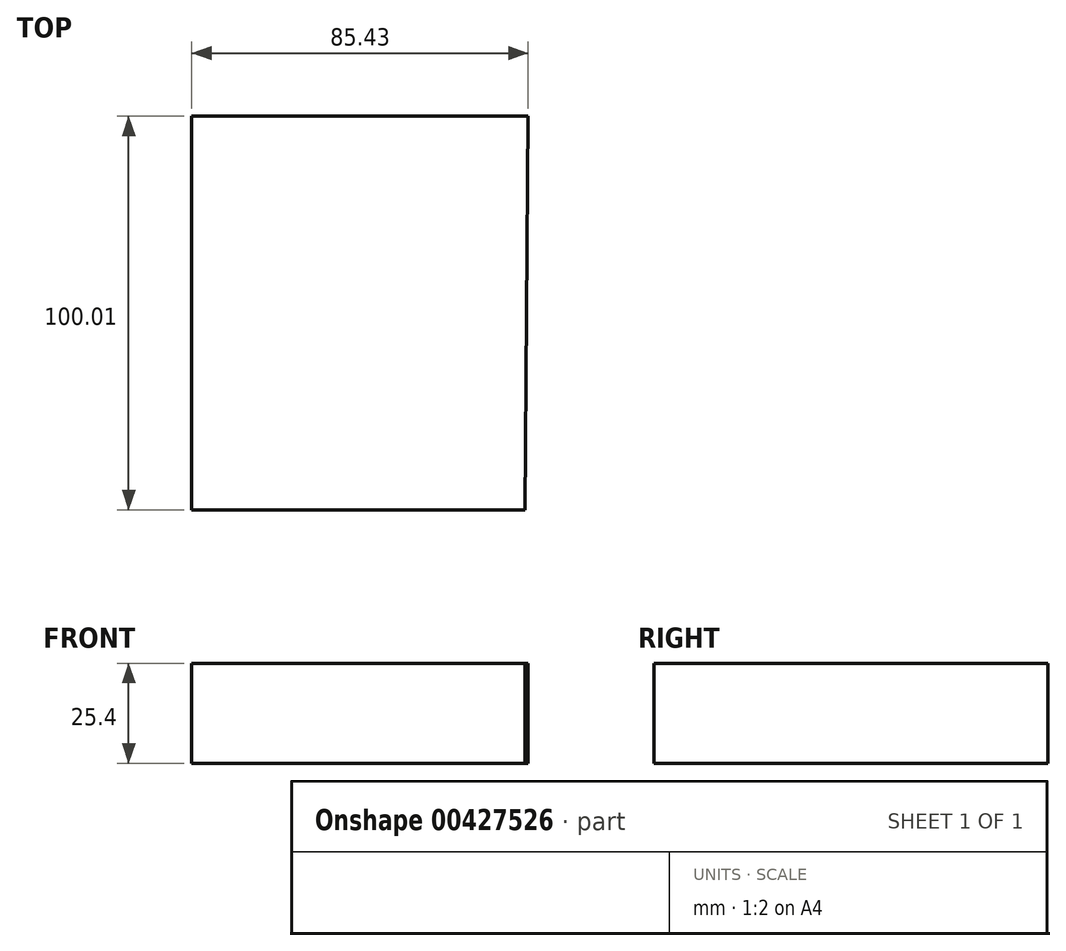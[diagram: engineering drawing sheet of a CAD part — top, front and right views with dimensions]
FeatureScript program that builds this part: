
annotation { "Feature Type Name" : "Feature", "Feature Type Description" : "" }
export const myFeature = defineFeature(function(context is Context, id is Id, definition is map)
    precondition{}
    {
        {
            var Q0;
            Q0=qCreatedBy(makeId("Top.planeOp"),FACE);
            var sketch = newSketch(context, id + "F0", { "sketchPlane" : qUnion([Q0])});
            skLineSegment(sketch, "E0", {"start": v(43.86, 41.62) * mm, "end": v(-41.57, 41.62) * mm});
            skLineSegment(sketch, "E1", {"start": v(-41.57, 41.62) * mm, "end": v(-41.57, -58.4) * mm});
            skLineSegment(sketch, "E2", {"start": v(-41.57, -58.4) * mm, "end": v(43.05, -58.4) * mm});
            skLineSegment(sketch, "E3", {"start": v(43.05, -58.4) * mm, "end": v(43.86, 41.62) * mm});
            skSolve(sketch);
        }
        {
            var Q0;
            Q0=makeQuery(id+"F0.imprint","IMPRINT",FACE,{"disambiguationData":[TD([[makeQuery(id+"F0.imprint","IMPRINT",EDGE,{"derivedFrom":sQuery(id+"F0.wireOp",EDGE,"E0")}),1.0]])]});
            var Q1;
            Q1=sQuery(id+"F0.wireOp",EDGE,"E0");
            var Q2;
            Q2=sQuery(id+"F0.wireOp",EDGE,"E2");
            var Q3;
            Q3=sQuery(id+"F0.wireOp",EDGE,"E3");
            var Q4;
            Q4=sQuery(id+"F0.wireOp",EDGE,"E1");
            extrude(context, id + "F1", {"entities" : qUnion([Q0]), "surfaceEntities" : qUnion([Q1, Q2, Q3, Q4]), "depth" : 25.4 * mm});
        }
    });
